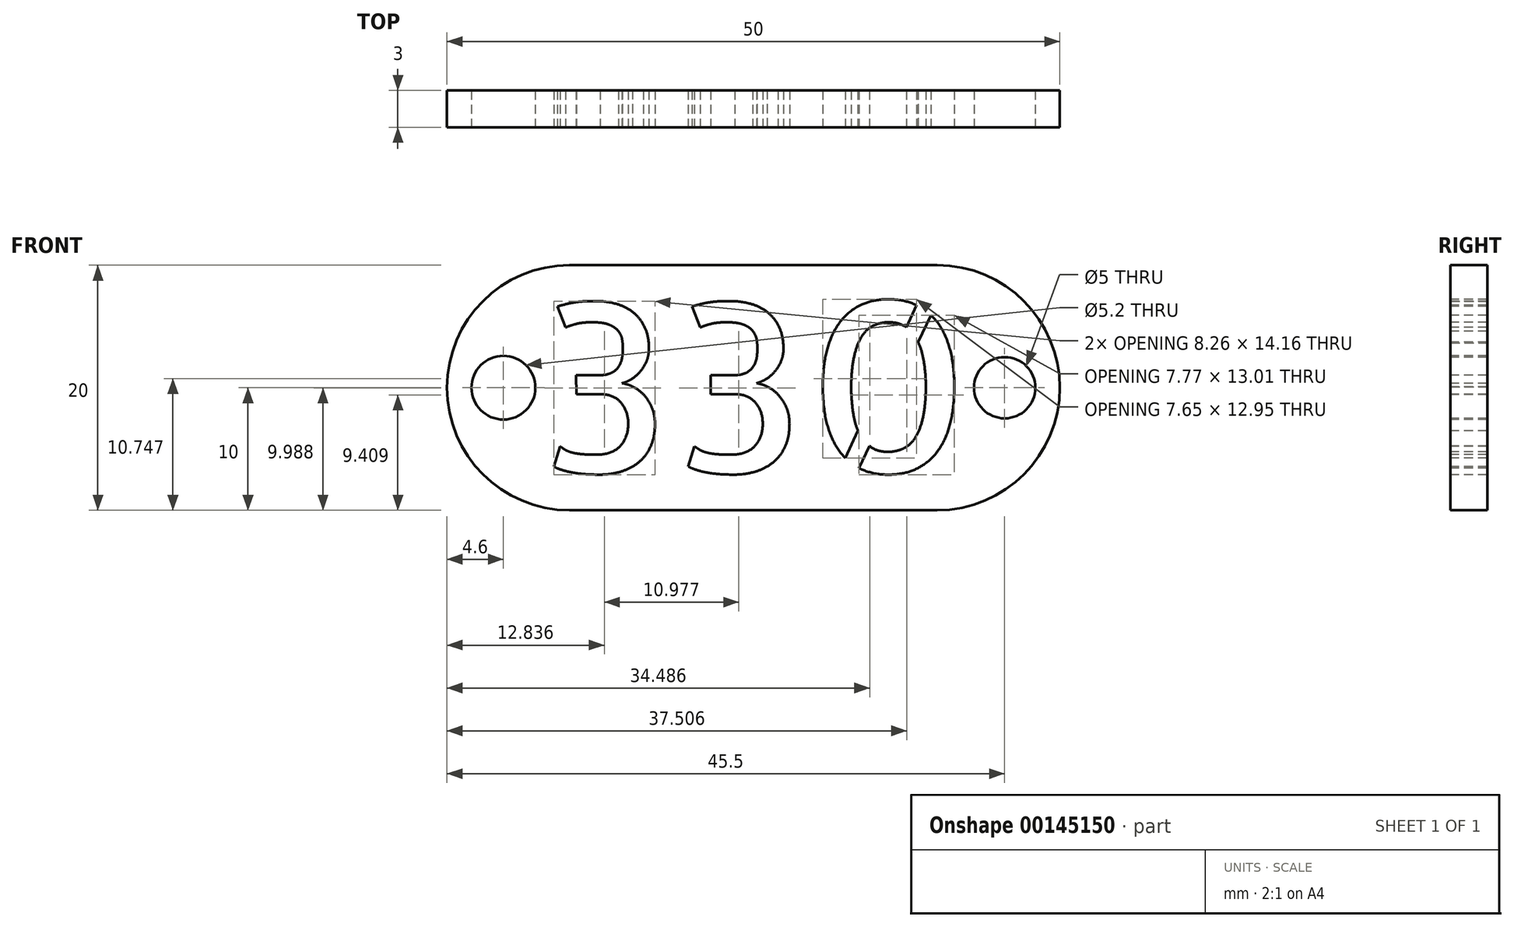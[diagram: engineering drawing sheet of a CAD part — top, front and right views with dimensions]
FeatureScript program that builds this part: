
annotation { "Feature Type Name" : "Feature", "Feature Type Description" : "" }
export const myFeature = defineFeature(function(context is Context, id is Id, definition is map)
    precondition{}
    {
        {
            var Q0;
            Q0=qCreatedBy(makeId("Front.planeOp"),FACE);
            var sketch = newSketch(context, id + "F0", { "sketchPlane" : qUnion([Q0])});
            skLineSegment(sketch, "E0.bottom", {"start": v(25, 10) * mm, "end": v(-25, 10) * mm});
            skLineSegment(sketch, "E0.top", {"start": v(25, -10) * mm, "end": v(-25, -10) * mm});
            skLineSegment(sketch, "E0.left", {"start": v(25, 10) * mm, "end": v(25, -10) * mm});
            skLineSegment(sketch, "E0.right", {"start": v(-25, 10) * mm, "end": v(-25, -10) * mm});
            skPoint(sketch, "E0.middle", {"position": v(0, 0) * mm});
            skSolve(sketch);
        }
        {
            var Q0;
            Q0=makeQuery(id+"F0.imprint","IMPRINT",FACE,{"disambiguationData":[TD([[makeQuery(id+"F0.imprint","IMPRINT",EDGE,{"derivedFrom":sQuery(id+"F0.wireOp",EDGE,"E0.bottom")}),1.0]])]});
            extrude(context, id + "F1", {"entities" : qUnion([Q0]), "depth" : 3 * mm});
        }
        {
            var Q0;
            Q0=makeQuery(id+"F1.opExtrude","CAP_FACE",FACE,{"disambiguationData":[OSD([sQuery(id+"F0.wireOp",EDGE,"E0.bottom"),sQuery(id+"F0.wireOp",EDGE,"E0.top"),sQuery(id+"F0.wireOp",EDGE,"E0.left"),sQuery(id+"F0.wireOp",EDGE,"E0.right")])],"isStart":false});
            var sketch = newSketch(context, id + "F2", { "sketchPlane" : qUnion([Q0])});
            skText(sketch, "E1", { "text": "330", "fontName": "AllertaStencil-Regular.ttf"});
            skLineSegment(sketch, "E2", {"start": v(-17.7, 0) * mm, "end": v(17.7, 0) * mm, "construction": true});
            skPoint(sketch, "E3", {"position": v(0, 0) * mm});
            skCircle(sketch, "E4", {"center": v(20.5, 0) * mm, "radius": 2.5 * mm});
            skCircle(sketch, "E5", {"center": v(-20.4, 0) * mm, "radius": 2.6 * mm});
            const initialGuessF2  = {"E1": [-0.0177, -0.007, 1, 0, 0.014]};
            skSetInitialGuess(sketch, initialGuessF2);
            skSolve(sketch);
        }
        {
            var Q0;
            Q0 = qSketchRegion(id + "F2", true);
            extrude(context, id + "F3", {"entities" : qUnion([Q0]), "operationType" : NewBodyOperationType.REMOVE, "endBound" : BoundingType.THROUGH_ALL, "oppositeDirection" : true, "depth" : 25 * mm});
        }
        {
            var Q0;
            Q0=makeQuery(id+"F1.opExtrude","SWEPT_EDGE",EDGE,{"disambiguationData":[OSD([sQuery(id+"F0.wireOp",EDGE,"E0.bottom"),sQuery(id+"F0.wireOp",EDGE,"E0.right")])]});
            var Q1;
            Q1=makeQuery(id+"F1.opExtrude","SWEPT_EDGE",EDGE,{"disambiguationData":[OSD([sQuery(id+"F0.wireOp",EDGE,"E0.top"),sQuery(id+"F0.wireOp",EDGE,"E0.right")])]});
            var Q2;
            Q2=makeQuery(id+"F1.opExtrude","SWEPT_EDGE",EDGE,{"disambiguationData":[OSD([sQuery(id+"F0.wireOp",EDGE,"E0.bottom"),sQuery(id+"F0.wireOp",EDGE,"E0.left")])]});
            var Q3;
            Q3=makeQuery(id+"F1.opExtrude","SWEPT_EDGE",EDGE,{"disambiguationData":[OSD([sQuery(id+"F0.wireOp",EDGE,"E0.top"),sQuery(id+"F0.wireOp",EDGE,"E0.left")])]});
            fillet(context, id + "F4", {"entities" : qUnion([Q0, Q1, Q2, Q3]), "radius" : 10 * mm, "tangentPropagation" : true, "allowEdgeOverflow" : false});
        }
    });
